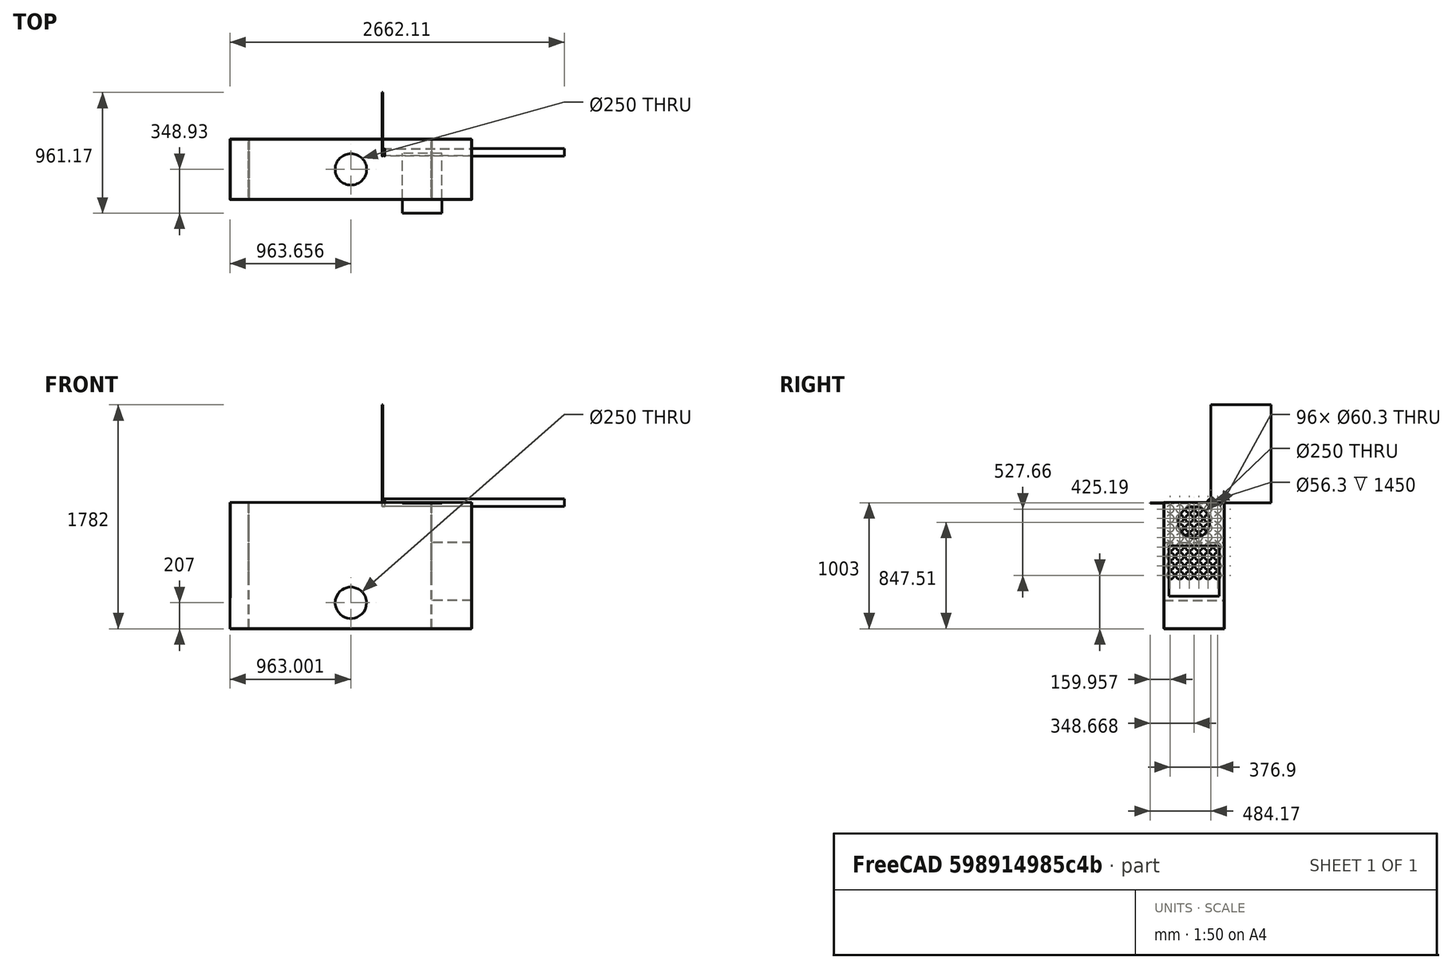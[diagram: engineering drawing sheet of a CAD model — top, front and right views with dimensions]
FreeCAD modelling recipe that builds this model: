
FCSTD DOCUMENT  (FreeCAD 0.19R24291 (Git))
Label: intercambiador_v4
License: All rights reserved
LicenseURL: http://en.wikipedia.org/wiki/All_rights_reserved
objects: TechDraw::DrawViewDimension×19, Part::Box×12, Part::Cylinder×7, Part::Cut×6, Part::Part2DObjectPython×6, TechDraw::DrawViewPart×6, Part::FeaturePython×4, Part::RuledSurface×4, Part::Extrusion×4, TechDraw::DrawSVGTemplate×4, TechDraw::DrawPage×4, Part::Refine×3, Part::MultiFuse×2, Sketcher::SketchObject×1, PartDesign::Pad×1, PartDesign::Body×1
note: 48 computed .brp shape members not serialized (recipe doc carries the construction recipe); baked Part::Feature solids carry a one-line shape summary decoded from their .brp

FEATURE [Sketcher::SketchObject] Sketch
  FullyConstrained = false
  MapMode = 5
  Placement = pos=(0,0,0) rot=(0.57735,0.57735,0.57735;2.0944rad)
  Support = -> [YZ_Plane]
  sketch-geometry (2):
    g0: Circle CenterX=0 CenterY=0 CenterZ=0 NormalX=0 NormalY=0 NormalZ=1 AngleXU=0 Radius=30.15
    g1: Circle CenterX=0 CenterY=0 CenterZ=0 NormalX=0 NormalY=0 NormalZ=1 AngleXU=0 Radius=28.15
  constraints (2):
    c: Diameter(g0) = 60.3
    c: Diameter(g1) = 56.3
FEATURE [PartDesign::Pad] Pad
  AllowMultiFace = false
  Direction = (1,1,1)
  Length = 1450
  Length2 = 100
  Placement = pos=(0,0,0) rot=(0.57735,0.57735,0.57735;2.0944rad)
  Profile = -> Sketch
  Type = 0
FEATURE [PartDesign::Body] Body  label="Caño"
  Group = -> [Sketch,Pad]
  Origin = -> Origin
  Tip = -> Pad
FEATURE [Part::Cylinder] Cylinder  label="Cilindro"
  Angle = 360
  AttacherType = Attacher::AttachEngine3D
  Height = 20
  Placement = pos=(0,0,0) rot=(0,1,0;1.5708rad)
  Radius = 30.15
FEATURE [Part::Box] Box  label="Chapa tubos"
  AttacherType = Attacher::AttachEngine3D
  Height = 779
  Length = 6
  Width = 477
FEATURE [Part::Box] Box001  label="Placa separadora"
  AttacherType = Attacher::AttachEngine3D
  Height = 477
  Length = 3
  Placement = pos=(476.059,-484.167,0) rot=(0.57735,-0.57735,-0.57735;4.18879rad)
  Width = 314
FEATURE [Part::FeaturePython] Array  label="Banco tubos"  # Draft array (typed FeaturePython)
  Angle = 360
  ArrayType = 0
  Axis = (0,0,1)
  Base = -> Body
  Center = (0,0,0)
  Count = 48
  ExpandArray = false
  Fuse = false
  IntervalAxis = (0,0,0)
  IntervalX = (100,0,0)
  IntervalY = (0,75.38,0)
  IntervalZ = (0,0,75.38)
  NumberCircles = 3
  NumberPolar = 5
  NumberX = 1
  NumberY = 6
  NumberZ = 8
  Placement = pos=(-1053.11,-324.213,-577.81) rot=(0,0,1;0rad)
  PlacementList = 48 placements: [(0,0,0),(0,0,75.38),(0,0,150.76),(0,0,226.14),(0,0,301.52),(0,0,376.9),(0,0,452.28),(0,0,527.66),(0,75.38,0),(0,75.38,75.38),(0,75.38,150.76),(0,75.38,226.14),(0,75.38,301.52),(0,75.38,376.9),(0,75.38,452.28),(0,75.38,527.66),(0,150.76,0),(0,150.76,75.38),(0,150.76,150.76),(0,150.76,226.14),(0,150.76,301.52),(0,150.76,376.9),(0,150.76,452.28),(0,150.76,527.66),(0,226.14,0),(0,226.14,75.38),+22 more]
  RadialDistance = 50
  ScaleList = (48) [(1,1,1),(1,1,1),(1,1,1),(1,1,1),(1,1,1),(1,1,1),(1,1,1),(1,1,1),(1,1,1),(1,1,1),(1,1,1),(1,1,1),(1,1,1),(1,1,1),(1,1,1),(1,1,1),(1,1,1),(1,1,1),+30 more]
  Symmetry = 1
  TangentialDistance = 25
FEATURE [Part::Cylinder] Cylinder001  label="Cilindro001"
  Angle = 360
  AttacherType = Attacher::AttachEngine3D
  Height = 20
  Placement = pos=(0,0,0) rot=(0.707107,0,0.707107;3.14159rad)
  Radius = 30.15
FEATURE [Part::FeaturePython] Array002  label="Mach"  # Draft array (typed FeaturePython)
  Angle = 360
  ArrayType = 0
  Axis = (0,0,1)
  Base = -> Cylinder001
  Center = (0,0,0)
  Count = 48
  ExpandArray = false
  Fuse = false
  IntervalAxis = (0,0,0)
  IntervalX = (100,0,0)
  IntervalY = (0,75.38,0)
  IntervalZ = (0,0,75.38)
  NumberCircles = 3
  NumberPolar = 5
  NumberX = 1
  NumberY = 6
  NumberZ = 8
  Placement = pos=(-9,50.15,50.15) rot=(0,0,1;0rad)
  PlacementList = <same value as first occurrence — deduplicated (x4 in doc)>
  RadialDistance = 50
  ScaleList = (48) [(1,1,1),(1,1,1),(1,1,1),(1,1,1),(1,1,1),(1,1,1),(1,1,1),(1,1,1),(1,1,1),(1,1,1),(1,1,1),(1,1,1),(1,1,1),(1,1,1),(1,1,1),(1,1,1),(1,1,1),(1,1,1),+30 more]
  Symmetry = 1
  TangentialDistance = 25
FEATURE [Part::Box] Box002  label="Chapa tubos001"
  AttacherType = Attacher::AttachEngine3D
  Height = 779
  Length = 6
  Width = 477
FEATURE [Part::Cylinder] Cylinder002  label="Cilindro002"
  Angle = 360
  AttacherType = Attacher::AttachEngine3D
  Height = 20
  Placement = pos=(0,0,0) rot=(0.707107,0,0.707107;3.14159rad)
  Radius = 30.15
FEATURE [Part::FeaturePython] Array003  label="Mach001"  # Draft array (typed FeaturePython)
  Angle = 360
  ArrayType = 0
  Axis = (0,0,1)
  Base = -> Cylinder002
  Center = (0,0,0)
  Count = 48
  ExpandArray = false
  Fuse = false
  IntervalAxis = (0,0,0)
  IntervalX = (100,0,0)
  IntervalY = (0,75.38,0)
  IntervalZ = (0,0,75.38)
  NumberCircles = 3
  NumberPolar = 5
  NumberX = 1
  NumberY = 6
  NumberZ = 8
  Placement = pos=(-9,50.15,50.15) rot=(0,0,1;0rad)
  PlacementList = <same value as first occurrence — deduplicated (x4 in doc)>
  RadialDistance = 50
  ScaleList = (48) [(1,1,1),(1,1,1),(1,1,1),(1,1,1),(1,1,1),(1,1,1),(1,1,1),(1,1,1),(1,1,1),(1,1,1),(1,1,1),(1,1,1),(1,1,1),(1,1,1),(1,1,1),(1,1,1),(1,1,1),(1,1,1),+30 more]
  Symmetry = 1
  TangentialDistance = 25
FEATURE [Part::Cut] Cut001  label="Placa tubos 2"
  Base = -> Box002
  Placement = pos=(390.891,102.837,0) rot=(1,0,0;3.14159rad)
  Tool = -> Array003
FEATURE [Part::Box] Box003  label="Placa separadora001"
  AttacherType = Attacher::AttachEngine3D
  Height = 477
  Length = 3
  Placement = pos=(710.891,-374.263,-313.98) rot=(0.57735,-0.57735,-0.57735;4.18879rad)
  Width = 314
FEATURE [Part::Box] Box004  label="Placa separadora002"
  AttacherType = Attacher::AttachEngine3D
  Height = 477
  Length = 3
  Placement = pos=(476.059,-484.167,0) rot=(0.57735,-0.57735,-0.57735;4.18879rad)
  Width = 314
FEATURE [Part::Box] Box005  label="tapa"
  AttacherType = Attacher::AttachEngine3D
  Height = 477
  Length = 3
  Placement = pos=(711.546,-373.74,3) rot=(0.57735,-0.57735,-0.57735;4.18879rad)
  Width = 1920
FEATURE [Part::Part2DObjectPython] Line  # Draft 2D object (typed FeaturePython)
  Area = 0
  ChamferSize = 0
  Closed = false
  End = (396.891,-324.213,-577.81)
  FilletRadius = 0
  Length = 527.66
  MakeFace = false
  Placement = pos=(396.891,-324.213,-50.15) rot=(0,0,1;0rad)
  Points = (2) [(0,0,0),(0,-5.68434e-14,-527.66)]
  Start = (396.891,-324.213,-50.15)
  Subdivisions = 0
FEATURE [Part::Part2DObjectPython] Line001  # Draft 2D object (typed FeaturePython)
  Area = 0
  ChamferSize = 0
  Closed = false
  End = (396.891,52.687,-577.81)
  FilletRadius = 0
  Length = 527.66
  MakeFace = false
  Placement = pos=(396.891,52.687,-50.15) rot=(0,0,1;0rad)
  Points = (2) [(0,0,0),(0,-6.39488e-14,-527.66)]
  Start = (396.891,52.687,-50.15)
  Subdivisions = 0
FEATURE [Part::Part2DObjectPython] Line002  # Draft 2D object (typed FeaturePython)
  Area = 0
  ChamferSize = 0
  Closed = false
  End = (396.891,52.687,-313.98)
  FilletRadius = 0
  Length = 376.9
  MakeFace = false
  Placement = pos=(396.891,-324.213,-313.98) rot=(0,0,1;0rad)
  Points = (2) [(0,0,0),(0,376.9,-5.68434e-14)]
  Start = (396.891,-324.213,-313.98)
  Subdivisions = 0
FEATURE [Part::Box] Box006  label="Chapa tubos002"
  AttacherType = Attacher::AttachEngine3D
  Height = 779
  Length = 6
  Width = 477
FEATURE [Part::Cylinder] Cylinder003  label="Cilindro003"
  Angle = 360
  AttacherType = Attacher::AttachEngine3D
  Height = 20
  Placement = pos=(0,0,0) rot=(0.707107,0,0.707107;3.14159rad)
  Radius = 30.15
FEATURE [Part::FeaturePython] Array004  label="Mach002"  # Draft array (typed FeaturePython)
  Angle = 360
  ArrayType = 0
  Axis = (0,0,1)
  Base = -> Cylinder003
  Center = (0,0,0)
  Count = 48
  ExpandArray = false
  Fuse = false
  IntervalAxis = (0,0,0)
  IntervalX = (100,0,0)
  IntervalY = (0,75.38,0)
  IntervalZ = (0,0,75.38)
  NumberCircles = 3
  NumberPolar = 5
  NumberX = 1
  NumberY = 6
  NumberZ = 8
  Placement = pos=(-9,50.15,50.15) rot=(0,0,1;0rad)
  PlacementList = <same value as first occurrence — deduplicated (x4 in doc)>
  RadialDistance = 50
  ScaleList = (48) [(1,1,1),(1,1,1),(1,1,1),(1,1,1),(1,1,1),(1,1,1),(1,1,1),(1,1,1),(1,1,1),(1,1,1),(1,1,1),(1,1,1),(1,1,1),(1,1,1),(1,1,1),(1,1,1),(1,1,1),(1,1,1),+30 more]
  Symmetry = 1
  TangentialDistance = 25
FEATURE [Part::Cut] Cut002  label="Placa tubos 1"
  Base = -> Box006
  Placement = pos=(-1065.11,102.837,-4.55e-13) rot=(1,0,0;3.14159rad)
  Tool = -> Array004
FEATURE [Part::Box] Box007  label="Base"
  AttacherType = Attacher::AttachEngine3D
  Height = 477
  Length = 3
  Placement = pos=(710.891,-374.163,-1000) rot=(0.57735,-0.57735,-0.57735;4.18879rad)
  Width = 1920
FEATURE [Part::Box] Box008  label="Placa separadora003"
  AttacherType = Attacher::AttachEngine3D
  Height = 477
  Length = 3
  Placement = pos=(710.891,-374.163,-776) rot=(0.57735,-0.57735,-0.57735;4.18879rad)
  Width = 314
FEATURE [Part::RuledSurface] Ruled_Surface  label="lateral trasera"
  Curve1 = -> Box007 [Edge3]
  Curve2 = -> Box005 [Edge3]
  Orientation = 0
FEATURE [Part::RuledSurface] Ruled_Surface001
  Curve1 = -> Box005 [Edge4]
  Curve2 = -> Box007 [Edge4]
  Orientation = 0
FEATURE [Part::RuledSurface] Ruled_Surface002
  Curve1 = -> Box005 [Edge1]
  Curve2 = -> Box007 [Edge1]
  Orientation = 0
FEATURE [Part::RuledSurface] Ruled_Surface003
  Curve1 = -> Box007 [Edge6]
  Curve2 = -> Box005 [Edge6]
  Orientation = 0
FEATURE [Part::Extrusion] Extrude002  label="cabezal trasero"
  Base = -> Ruled_Surface
  Dir = (-1,0,0)
  DirMode = 0
  FaceMakerClass = Part::FaceMakerBullseye
  LengthFwd = 3
  LengthRev = 0
  Solid = false
  Symmetric = false
FEATURE [Part::Extrusion] Extrude  label="Lateral izq"
  Base = -> Ruled_Surface001
  Dir = (0,-1,0)
  DirMode = 0
  FaceMakerClass = Part::FaceMakerBullseye
  LengthFwd = 3
  LengthRev = 0
  Solid = false
  Symmetric = false
FEATURE [Part::Extrusion] Extrude004  label="Lateral der"
  Base = -> Ruled_Surface003
  Dir = (0,1,0)
  DirMode = 0
  FaceMakerClass = Part::FaceMakerBullseye
  LengthFwd = 3
  LengthRev = 0
  Solid = false
  Symmetric = false
FEATURE [Part::Cylinder] Cylinder006  label="Cilindro006"
  Angle = 360
  AttacherType = Attacher::AttachEngine3D
  Height = 60
  Placement = pos=(691.219,-135.501,-155.49) rot=(0,1,0;1.5708rad)
  Radius = 125
FEATURE [Part::Part2DObjectPython] Line003  # Draft 2D object (typed FeaturePython)
  Area = 0
  ChamferSize = 0
  Closed = false
  End = (710.891,-135.763,-313.98)
  FilletRadius = 0
  Length = 316.981
  MakeFace = false
  Placement = pos=(711.546,-135.24,3) rot=(0,0,1;0rad)
  Points = (2) [(0,0,0),(-0.655294,-0.52307,-316.98)]
  Start = (711.546,-135.24,3)
  Subdivisions = 0
FEATURE [Part::Box] Box009  label="Cubo"
  AttacherType = Attacher::AttachEngine3D
  Height = 400
  Length = 80
  Placement = pos=(650.891,-335.713,-744.99) rot=(0,0,1;0rad)
  Width = 400
FEATURE [Part::Part2DObjectPython] Line004  # Draft 2D object (typed FeaturePython)
  Area = 0
  ChamferSize = 0
  Closed = false
  End = (710.891,-135.663,-776)
  FilletRadius = 0
  Length = 462.02
  MakeFace = false
  Placement = pos=(710.891,-135.763,-313.98) rot=(0,0,1;0rad)
  Points = (2) [(0,0,0),(0,0.1,-462.02)]
  Start = (710.891,-135.763,-313.98)
  Subdivisions = 0
FEATURE [Part::Part2DObjectPython] Line005  # Draft 2D object (typed FeaturePython)
  Area = 0
  ChamferSize = 0
  Closed = false
  End = (-249.109,-377.163,-706)
  FilletRadius = 0
  Length = 70
  MakeFace = false
  Placement = pos=(-249.109,-377.163,-776) rot=(0,0,1;0rad)
  Points = (2) [(0,0,0),(0,0,70)]
  Start = (-249.109,-377.163,-776)
  Subdivisions = 0
FEATURE [Part::Cylinder] Cylinder007  label="Cilindro007"
  Angle = 360
  AttacherType = Attacher::AttachEngine3D
  Height = 70
  Placement = pos=(-249.109,-350.16,-796) rot=(1,0,0;1.5708rad)
  Radius = 125
FEATURE [Part::Cut] Cut004  label="lateral izq"
  Base = -> Extrude
  Tool = -> Cylinder007
FEATURE [Part::Cylinder] Cylinder008  label="Cilindro008"
  Angle = 360
  AttacherType = Attacher::AttachEngine3D
  Height = 60
  Placement = pos=(-248.454,-135.24,-50) rot=(0,0,1;1.5708rad)
  Radius = 125
FEATURE [Part::Cut] Cut005  label="Tapa"
  Base = -> Box005
  Tool = -> Cylinder008
FEATURE [TechDraw::DrawSVGTemplate] Template
  EditableTexts = APPROVER_NAME=APPROVER NAME,AUTHOR_NAME=AUTHOR NAME,DATE=YYYY-MM-DD,DN=DN,DOCUMENT_TYPE=Mechanical assembly drawing,OWNER_NAME=OWNER NAME,PM=PM,PN=PN,+7 more (map truncated)
  Height = 210
  Orientation = 1
  Width = 297
FEATURE [Part::Extrusion] Extrude003  label="cabezal frontal"
  Base = -> Ruled_Surface002
  Dir = (1,0,0)
  DirMode = 0
  FaceMakerClass = Part::FaceMakerBullseye
  LengthFwd = 3
  LengthRev = 0
  Solid = false
  Symmetric = false
FEATURE [Part::Cut] Cut
  Base = -> Extrude003
  Tool = -> Cylinder006
FEATURE [Part::Cut] Cut003  label="cabezal front"
  Base = -> Cut
  Tool = -> Box009
FEATURE [TechDraw::DrawViewPart] View  label="Cabezal Frontal"
  CoarseView = false
  Direction = (1,0,0)
  Focus = 100
  HardHidden = false
  IsoCount = 0
  IsoHidden = false
  IsoVisible = false
  LockPosition = false
  Perspective = false
  Rotation = 0
  Scale = 0.12
  ScaleType = 0
  SeamHidden = false
  SeamVisible = true
  SmoothHidden = false
  SmoothVisible = true
  Source = -> [Cut003]
  X = 52.7481
  XDirection = (0,1,0)
  Y = 114.029
FEATURE [TechDraw::DrawViewDimension] Dimension
  Arbitrary = false
  ArbitraryTolerances = false
  EqualTolerance = true
  FormatSpec = %.2f
  FormatSpecOverTolerance = %+.2f
  FormatSpecUnderTolerance = %+.2f
  Inverted = false
  LockPosition = false
  MeasureType = 1
  OverTolerance = 0
  References2D = -> [View]
  Rotation = 0
  ScaleType = 0
  TheoreticalExact = false
  Type = 1
  UnderTolerance = 0
  X = 0.846231
  Y = 68.7989
FEATURE [TechDraw::DrawViewDimension] Dimension001
  Arbitrary = false
  ArbitraryTolerances = false
  EqualTolerance = true
  FormatSpec = %.2f
  FormatSpecOverTolerance = %+.2f
  FormatSpecUnderTolerance = %+.2f
  Inverted = false
  LockPosition = false
  MeasureType = 1
  OverTolerance = 0
  References2D = -> [View]
  Rotation = 0
  ScaleType = 0
  TheoreticalExact = false
  Type = 2
  UnderTolerance = 0
  X = 36.418
  Y = 0
FEATURE [TechDraw::DrawViewDimension] Dimension002
  Arbitrary = false
  ArbitraryTolerances = false
  EqualTolerance = true
  FormatSpec = ⌀%.2f
  FormatSpecOverTolerance = %+.2f
  FormatSpecUnderTolerance = %+.2f
  Inverted = false
  LockPosition = false
  MeasureType = 1
  OverTolerance = 0
  References2D = -> [View]
  Rotation = 0
  ScaleType = 0
  TheoreticalExact = false
  Type = 5
  UnderTolerance = 0
  X = -1.64169
  Y = 46.3779
FEATURE [TechDraw::DrawViewDimension] Dimension003
  Arbitrary = false
  ArbitraryTolerances = false
  EqualTolerance = true
  FormatSpec = %.2f
  FormatSpecOverTolerance = %+.2f
  FormatSpecUnderTolerance = %+.2f
  Inverted = false
  LockPosition = false
  MeasureType = 1
  OverTolerance = 0
  References2D = -> [View]
  Rotation = 0
  ScaleType = 0
  TheoreticalExact = false
  Type = 1
  UnderTolerance = 0
  X = 0.789463
  Y = -35.3247
FEATURE [TechDraw::DrawViewDimension] Dimension004
  Arbitrary = false
  ArbitraryTolerances = false
  EqualTolerance = true
  FormatSpec = %.2f
  FormatSpecOverTolerance = %+.2f
  FormatSpecUnderTolerance = %+.2f
  Inverted = false
  LockPosition = false
  MeasureType = 1
  OverTolerance = 0
  References2D = -> [View]
  Rotation = 0
  ScaleType = 0
  TheoreticalExact = false
  Type = 2
  UnderTolerance = 0
  X = -40.4679
  Y = -7.63092
FEATURE [TechDraw::DrawSVGTemplate] Template001
  EditableTexts = AUTHOR_NAME=AUTHOR NAME,DN=DN,DRAWING_TITLE=DRAWING TITLE,FC-DATE=DD/MM/YYYY,FC-REV=REV A,FC-SC=SCALE,FC-SH=X / Y,FC-SI=A4,+2 more (map truncated)
  Height = 210
  Orientation = 1
  Width = 297
FEATURE [Part::Box] Box010  label="Cubo001"
  AttacherType = Attacher::AttachEngine3D
  Height = 221
  Length = 6
  Placement = pos=(390.891,-374.163,-1000) rot=(0,0,1;0rad)
  Width = 477
FEATURE [Part::MultiFuse] Fusion
  Shapes = -> [Cut001,Box010]
FEATURE [Part::Box] Box011  label="Cubo002"
  AttacherType = Attacher::AttachEngine3D
  Height = 221
  Length = 6
  Placement = pos=(-1065.11,-374.163,-1000) rot=(0,0,1;0rad)
  Width = 477
FEATURE [Part::MultiFuse] Fusion001
  Shapes = -> [Cut002,Box011]
FEATURE [Part::Refine] Fusion001001
  Source = -> Fusion001
FEATURE [Part::Refine] Fusion001002
  Source = -> Fusion
FEATURE [TechDraw::DrawViewPart] View004  label="Placa Porta Tubos"
  CoarseView = false
  Direction = (1,0,0)
  Focus = 100
  HardHidden = false
  IsoCount = 0
  IsoHidden = false
  IsoVisible = false
  LockPosition = false
  Perspective = false
  Rotation = 180
  Scale = 0.12
  ScaleType = 0
  SeamHidden = false
  SeamVisible = true
  SmoothHidden = false
  SmoothVisible = true
  Source = -> [Fusion001002,Box003]
  X = 147.737
  XDirection = (0,-1,0)
  Y = 113.009
FEATURE [TechDraw::DrawViewDimension] Dimension014
  Arbitrary = false
  ArbitraryTolerances = false
  EqualTolerance = true
  FormatSpec = %.2f
  FormatSpecOverTolerance = %+.2f
  FormatSpecUnderTolerance = %+.2f
  Inverted = false
  LockPosition = false
  MeasureType = 1
  OverTolerance = 0
  References2D = -> [View004]
  Rotation = 0
  ScaleType = 0
  TheoreticalExact = false
  Type = 2
  UnderTolerance = 0
  X = 39.5504
  Y = 0
FEATURE [TechDraw::DrawViewDimension] Dimension015
  Arbitrary = false
  ArbitraryTolerances = false
  EqualTolerance = true
  FormatSpec = %.2f
  FormatSpecOverTolerance = %+.2f
  FormatSpecUnderTolerance = %+.2f
  Inverted = false
  LockPosition = false
  MeasureType = 1
  OverTolerance = 0
  References2D = -> [View004]
  Rotation = 0
  ScaleType = 0
  TheoreticalExact = false
  Type = 1
  UnderTolerance = 0
  X = 0.006
  Y = 68.7713
FEATURE [TechDraw::DrawViewDimension] Dimension016
  Arbitrary = false
  ArbitraryTolerances = false
  EqualTolerance = true
  FormatSpec = ⌀%.2f
  FormatSpecOverTolerance = %+.2f
  FormatSpecUnderTolerance = %+.2f
  Inverted = false
  LockPosition = false
  MeasureType = 1
  OverTolerance = 0
  References2D = -> [View004]
  Rotation = 0
  ScaleType = 0
  TheoreticalExact = false
  Type = 5
  UnderTolerance = 0
  X = -37.7549
  Y = 41.5685
FEATURE [TechDraw::DrawViewDimension] Dimension017
  Arbitrary = false
  ArbitraryTolerances = false
  EqualTolerance = true
  FormatSpec = %.2f
  FormatSpecOverTolerance = %+.2f
  FormatSpecUnderTolerance = %+.2f
  Inverted = false
  LockPosition = false
  MeasureType = 1
  OverTolerance = 0
  References2D = -> [View004]
  Rotation = 0
  ScaleType = 0
  TheoreticalExact = false
  Type = 2
  UnderTolerance = 0
  X = -38.1541
  Y = -16.7306
FEATURE [TechDraw::DrawViewDimension] Dimension018
  Arbitrary = false
  ArbitraryTolerances = false
  EqualTolerance = true
  FormatSpec = %.2f
  FormatSpecOverTolerance = %+.2f
  FormatSpecUnderTolerance = %+.2f
  Inverted = false
  LockPosition = false
  MeasureType = 1
  OverTolerance = 0
  References2D = -> [View004]
  Rotation = 0
  ScaleType = 0
  TheoreticalExact = false
  Type = 2
  UnderTolerance = 0
  X = 34.3625
  Y = 32.5593
FEATURE [TechDraw::DrawViewPart] View005  label="Placa Porta Tubos Trasera"
  CoarseView = false
  Direction = (-1,0,0)
  Focus = 100
  HardHidden = false
  IsoCount = 0
  IsoHidden = false
  IsoVisible = false
  LockPosition = false
  Perspective = false
  Rotation = 0
  Scale = 0.12
  ScaleType = 0
  SeamHidden = false
  SeamVisible = true
  SmoothHidden = false
  SmoothVisible = true
  Source = -> [Fusion001002]
  X = 242.45
  XDirection = (0,-1,0)
  Y = 113.588
FEATURE [TechDraw::DrawViewDimension] Dimension019
  Arbitrary = false
  ArbitraryTolerances = false
  EqualTolerance = true
  FormatSpec = %.2f
  FormatSpecOverTolerance = %+.2f
  FormatSpecUnderTolerance = %+.2f
  Inverted = false
  LockPosition = false
  MeasureType = 1
  OverTolerance = 0
  References2D = -> [View005]
  Rotation = 0
  ScaleType = 0
  TheoreticalExact = false
  Type = 1
  UnderTolerance = 0
  X = -3.76556
  Y = -18.1602
FEATURE [TechDraw::DrawViewDimension] Dimension020
  Arbitrary = false
  ArbitraryTolerances = false
  EqualTolerance = true
  FormatSpec = %.2f
  FormatSpecOverTolerance = %+.2f
  FormatSpecUnderTolerance = %+.2f
  Inverted = false
  LockPosition = false
  MeasureType = 1
  OverTolerance = 0
  References2D = -> [View005]
  Rotation = 0
  ScaleType = 0
  TheoreticalExact = false
  Type = 2
  UnderTolerance = 0
  X = 35.1179
  Y = -17.8013
FEATURE [TechDraw::DrawPage] Page  label="Vistas frontales"
  KeepUpdated = true
  NextBalloonIndex = 1
  ProjectionType = 0
  Template = -> Template
  Views = -> [View,Dimension,Dimension001,Dimension002,Dimension003,Dimension004,View004,Dimension014,Dimension015,Dimension016,Dimension017,Dimension018,View005,Dimension019,Dimension020]
FEATURE [TechDraw::DrawViewPart] View006  label="Lateral Izquierdo"
  CoarseView = false
  Direction = (0,-1,0)
  Focus = 100
  HardHidden = false
  IsoCount = 0
  IsoHidden = false
  IsoVisible = false
  LockPosition = false
  Perspective = false
  Rotation = 0
  Scale = 0.12
  ScaleType = 0
  SeamHidden = false
  SeamVisible = true
  SmoothHidden = false
  SmoothVisible = true
  Source = -> [Extrude002,Extrude004,Box003,Cut003,Cut005,Fusion001001,Fusion001002,Array,Box007]
  X = 147.032
  XDirection = (1,0,0)
  Y = 118.319
FEATURE [TechDraw::DrawViewDimension] Dimension022
  Arbitrary = false
  ArbitraryTolerances = false
  EqualTolerance = true
  FormatSpec = %.2f
  FormatSpecOverTolerance = %+.2f
  FormatSpecUnderTolerance = %+.2f
  Inverted = false
  LockPosition = false
  MeasureType = 1
  OverTolerance = 0
  References2D = -> [View006]
  Rotation = 0
  Scale = 0.12
  ScaleType = 0
  TheoreticalExact = false
  Type = 2
  UnderTolerance = 0
  X = 127.538
  Y = -20.0794
FEATURE [TechDraw::DrawViewDimension] Dimension023
  Arbitrary = false
  ArbitraryTolerances = false
  EqualTolerance = true
  FormatSpec = %.2f
  FormatSpecOverTolerance = %+.2f
  FormatSpecUnderTolerance = %+.2f
  Inverted = false
  LockPosition = false
  MeasureType = 1
  OverTolerance = 0
  References2D = -> [View006]
  Rotation = 0
  Scale = 0.12
  ScaleType = 0
  TheoreticalExact = false
  Type = 2
  UnderTolerance = 0
  X = 127.927
  Y = 37.7994
FEATURE [TechDraw::DrawViewDimension] Dimension024
  Arbitrary = false
  ArbitraryTolerances = false
  EqualTolerance = true
  FormatSpec = %.2f
  FormatSpecOverTolerance = %+.2f
  FormatSpecUnderTolerance = %+.2f
  Inverted = false
  LockPosition = false
  MeasureType = 1
  OverTolerance = 0
  References2D = -> [View006]
  Rotation = 0
  Scale = 0.12
  ScaleType = 0
  TheoreticalExact = false
  Type = 2
  UnderTolerance = 0
  X = -130.673
  Y = 24.3615
FEATURE [TechDraw::DrawViewDimension] Dimension026
  Arbitrary = false
  ArbitraryTolerances = false
  EqualTolerance = true
  FormatSpec = %.2f
  FormatSpecOverTolerance = %+.2f
  FormatSpecUnderTolerance = %+.2f
  Inverted = false
  LockPosition = false
  MeasureType = 1
  OverTolerance = 0
  References2D = -> [View006]
  Rotation = 0
  Scale = 0.12
  ScaleType = 0
  TheoreticalExact = false
  Type = 1
  UnderTolerance = 0
  X = -8.35003
  Y = 68.305
FEATURE [TechDraw::DrawViewDimension] Dimension027
  Arbitrary = false
  ArbitraryTolerances = false
  EqualTolerance = true
  FormatSpec = %.2f
  FormatSpecOverTolerance = %+.2f
  FormatSpecUnderTolerance = %+.2f
  Inverted = false
  LockPosition = false
  MeasureType = 1
  OverTolerance = 0
  References2D = -> [View006]
  Rotation = 0
  Scale = 0.12
  ScaleType = 0
  TheoreticalExact = false
  Type = 1
  UnderTolerance = 0
  X = 57.9191
  Y = -42.6681
FEATURE [TechDraw::DrawViewDimension] Dimension028
  Arbitrary = false
  ArbitraryTolerances = false
  EqualTolerance = true
  FormatSpec = %.2f
  FormatSpecOverTolerance = %+.2f
  FormatSpecUnderTolerance = %+.2f
  Inverted = false
  LockPosition = false
  MeasureType = 1
  OverTolerance = 0
  References2D = -> [View006]
  Rotation = 0
  Scale = 0.12
  ScaleType = 0
  TheoreticalExact = false
  Type = 1
  UnderTolerance = 0
  X = -106.239
  Y = -61.7093
FEATURE [TechDraw::DrawViewDimension] Dimension029
  Arbitrary = false
  ArbitraryTolerances = false
  EqualTolerance = true
  FormatSpec = %.2f
  FormatSpecOverTolerance = %+.2f
  FormatSpecUnderTolerance = %+.2f
  Inverted = false
  LockPosition = false
  MeasureType = 1
  OverTolerance = 0
  References2D = -> [View006]
  Rotation = 0
  Scale = 0.12
  ScaleType = 0
  TheoreticalExact = false
  Type = 1
  UnderTolerance = 0
  X = 98.5488
  Y = 68.666
FEATURE [TechDraw::DrawPage] Page001  label="Vista Lateral 1"
  KeepUpdated = true
  NextBalloonIndex = 1
  ProjectionType = 0
  Scale = 0.12
  Template = -> Template001
  Views = -> [View006,Dimension022,Dimension023,Dimension024,Dimension026,Dimension027,Dimension028,Dimension029]
FEATURE [TechDraw::DrawSVGTemplate] Template003
  EditableTexts = AUTHOR_NAME=AUTHOR NAME; DN=DN; DRAWING_TITLE=DRAWING TITLE; FC-DATE=DD/MM/YYYY; FC-REV=REV A; FC-SC=SCALE; FC-SH=X / Y; FC-SI=A4; FreeCAD_DRAWING=FreeCAD DRAWING; PN=PN
  Height = 210
  Orientation = 1
  Width = 297
FEATURE [TechDraw::DrawViewPart] View008
  CoarseView = false
  Direction = (0,-1,0)
  Focus = 100
  HardHidden = false
  IsoCount = 0
  IsoHidden = false
  IsoVisible = false
  LockPosition = false
  Perspective = false
  Rotation = 0
  Scale = 0.12
  ScaleType = 0
  SeamHidden = false
  SeamVisible = true
  SmoothHidden = false
  SmoothVisible = true
  Source = -> [Cut004,Extrude004]
  X = 151.578
  XDirection = (1,0,0)
  Y = 122.101
FEATURE [TechDraw::DrawPage] Page003
  KeepUpdated = true
  NextBalloonIndex = 1
  ProjectionType = 0
  Template = -> Template003
  Views = -> [View008]
FEATURE [Part::Refine] Cut004001001  label="lateral izq002"
FEATURE [TechDraw::DrawSVGTemplate] Template004
  EditableTexts = AUTHOR_NAME=AUTHOR NAME; DN=DN; DRAWING_TITLE=DRAWING TITLE; FC-DATE=DD/MM/YYYY; FC-REV=REV A; FC-SC=SCALE; FC-SH=X / Y; FC-SI=A3; FreeCAD_DRAWING=FreeCAD DRAWING; PN=PN
  Height = 297
  Orientation = 1
  Width = 420
FEATURE [TechDraw::DrawViewPart] View009  label="Intercambiador"
  CoarseView = false
  Direction = (0.577,-0.577,0.577)
  Focus = 100
  HardHidden = false
  IsoCount = 0
  IsoHidden = false
  IsoVisible = false
  LockPosition = false
  Perspective = false
  Rotation = 0
  Scale = 0.1
  ScaleType = 0
  SeamHidden = false
  SeamVisible = true
  SmoothHidden = false
  SmoothVisible = true
  Source = -> [Cut005,Cut004,Cut003,Extrude004,Box007,Extrude002,Array,Box003,Fusion001001,Fusion001002]
  X = 316.417
  XDirection = (0.707,0.707,0)
  Y = 190.099
FEATURE [TechDraw::DrawPage] Page004  label="Equipo"
  KeepUpdated = true
  NextBalloonIndex = 1
  ProjectionType = 0
  Template = -> Template004
  Views = -> [View009]
